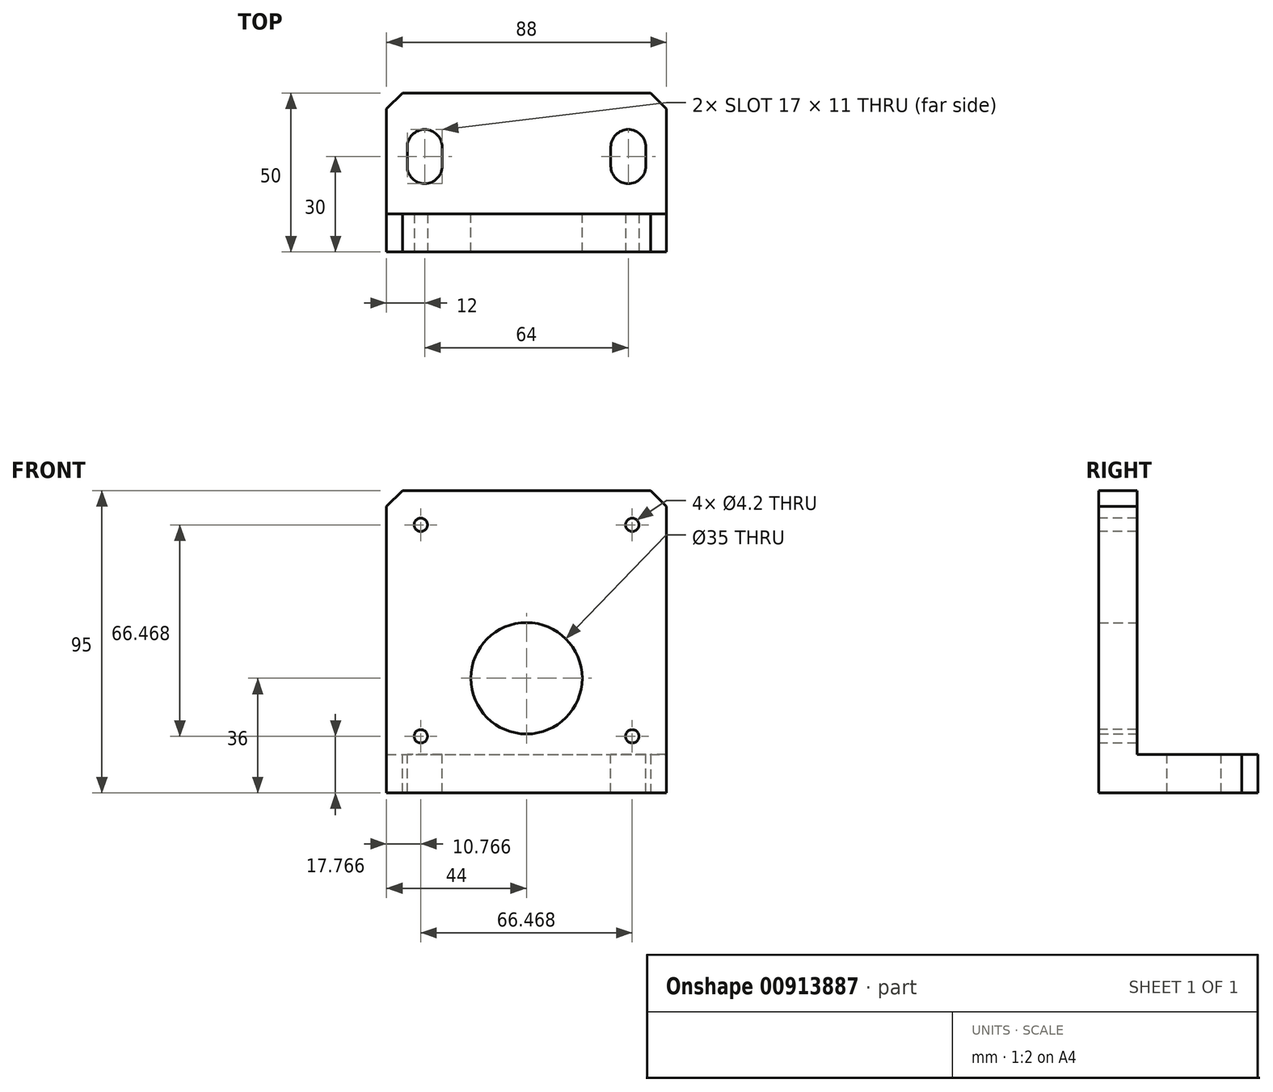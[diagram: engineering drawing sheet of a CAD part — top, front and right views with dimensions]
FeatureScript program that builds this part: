
annotation { "Feature Type Name" : "Feature", "Feature Type Description" : "" }
export const myFeature = defineFeature(function(context is Context, id is Id, definition is map)
    precondition{}
    {
        {
            var Q0;
            Q0=qCreatedBy(makeId("Front.planeOp"),FACE);
            var sketch = newSketch(context, id + "F0", { "sketchPlane" : qUnion([Q0])});
            skLineSegment(sketch, "E0.bottom", {"start": v(-44, 0) * mm, "end": v(44, 0) * mm});
            skLineSegment(sketch, "E0.top", {"start": v(-44, 95) * mm, "end": v(44, 95) * mm});
            skLineSegment(sketch, "E0.left", {"start": v(-44, 0) * mm, "end": v(-44, 95) * mm});
            skLineSegment(sketch, "E0.right", {"start": v(44, 0) * mm, "end": v(44, 95) * mm});
            skCircle(sketch, "E1", {"center": v(0, 36) * mm, "radius": 17.5 * mm});
            skSolve(sketch);
        }
        {
            var Q0;
            Q0 = qSketchRegion(id + "F0", true);
            extrude(context, id + "F1", {"entities" : qUnion([Q0]), "depth" : 12 * mm, "offsetDistance" : 25 * mm});
        }
        {
            var Q0;
            Q0=makeQuery(id+"F1.opExtrude","CAP_FACE",FACE,{"disambiguationData":[OSD([sQuery(id+"F0.wireOp",EDGE,"E0.bottom"),sQuery(id+"F0.wireOp",EDGE,"E0.top"),sQuery(id+"F0.wireOp",EDGE,"E0.left"),sQuery(id+"F0.wireOp",EDGE,"E0.right"),sQuery(id+"F0.wireOp",EDGE,"E1")])],"isStart":true});
            var sketch = newSketch(context, id + "F2", { "sketchPlane" : qUnion([Q0])});
            skLineSegment(sketch, "E2.bottom", {"start": v(44, 0) * mm, "end": v(-44, 0) * mm});
            skLineSegment(sketch, "E2.top", {"start": v(44, 12) * mm, "end": v(-44, 12) * mm});
            skLineSegment(sketch, "E2.left", {"start": v(44, 0) * mm, "end": v(44, 12) * mm});
            skLineSegment(sketch, "E2.right", {"start": v(-44, 0) * mm, "end": v(-44, 12) * mm});
            skSolve(sketch);
        }
        {
            var Q0;
            Q0 = qSketchRegion(id + "F2", true);
            extrude(context, id + "F3", {"entities" : qUnion([Q0]), "operationType" : NewBodyOperationType.ADD, "depth" : 38 * mm, "offsetDistance" : 25 * mm});
        }
        {
            var Q0;
            Q0=makeQuery(id+"F3.opExtrude","SWEPT_FACE",FACE,{"disambiguationData":[OSD([sQuery(id+"F2.wireOp",EDGE,"E2.top")])]});
            var sketch = newSketch(context, id + "F4", { "sketchPlane" : qUnion([Q0])});
            skLineSegment(sketch, "E3", {"start": v(32, 15) * mm, "end": v(32, 21) * mm, "construction": true});
            skLineSegment(sketch, "E4.0", {"start": v(37.5, 15) * mm, "end": v(37.5, 21) * mm});
            skLineSegment(sketch, "E5.0", {"start": v(26.5, 15) * mm, "end": v(26.5, 21) * mm});
            skArc(sketch, "E6", {"start": v(26.5, 15) * mm, "mid": v(32, 9.5) * mm, "end": v(37.5, 15) * mm});
            skArc(sketch, "E7", {"start": v(26.5, 21) * mm, "mid": v(32, 26.5) * mm, "end": v(37.5, 21) * mm});
            skLineSegment(sketch, "E8", {"start": v(0, 0) * mm, "end": v(0, 38) * mm, "construction": true});
            skLineSegment(sketch, "E9.MirrorCS", {"start": v(-26.5, 15) * mm, "end": v(-26.5, 21) * mm});
            skLineSegment(sketch, "E10.MirrorCS", {"start": v(-32, 15) * mm, "end": v(-32, 21) * mm, "construction": true});
            skLineSegment(sketch, "E11.MirrorCS", {"start": v(-37.5, 15) * mm, "end": v(-37.5, 21) * mm});
            skArc(sketch, "E12.MirrorCS", {"start": v(-26.5, 15) * mm, "mid": v(-32, 9.5) * mm, "end": v(-37.5, 15) * mm});
            skArc(sketch, "E13.MirrorCS", {"start": v(-26.5, 21) * mm, "mid": v(-32, 26.5) * mm, "end": v(-37.5, 21) * mm});
            skSolve(sketch);
        }
        {
            var Q0;
            Q0 = qSketchRegion(id + "F4", true);
            extrude(context, id + "F5", {"entities" : qUnion([Q0]), "operationType" : NewBodyOperationType.REMOVE, "endBound" : BoundingType.UP_TO_NEXT, "oppositeDirection" : true, "depth" : 25 * mm, "offsetDistance" : 25 * mm});
        }
        {
            var Q0;
            Q0=makeQuery(id+"F1.opExtrude","CAP_FACE",FACE,{"disambiguationData":[OSD([sQuery(id+"F0.wireOp",EDGE,"E0.bottom"),sQuery(id+"F0.wireOp",EDGE,"E0.top"),sQuery(id+"F0.wireOp",EDGE,"E0.left"),sQuery(id+"F0.wireOp",EDGE,"E0.right"),sQuery(id+"F0.wireOp",EDGE,"E1")])],"isStart":false});
            var sketch = newSketch(context, id + "F6", { "sketchPlane" : qUnion([Q0])});
            skCircle(sketch, "E14", {"center": v(0, 51) * mm, "radius": 47 * mm, "construction": true});
            skLineSegment(sketch, "E15", {"start": v(0, 51) * mm, "end": v(-33.23, 84.23) * mm, "construction": true});
            skPoint(sketch, "E16", {"position": v(-33.23, 84.23) * mm});
            skPoint(sketch, "E17.1.0", {"position": v(33.23, 84.23) * mm});
            skPoint(sketch, "E17.2.0", {"position": v(33.23, 17.77) * mm});
            skPoint(sketch, "E17.3.0", {"position": v(-33.23, 17.77) * mm});
            skLineSegment(sketch, "E17.anchor2", {"start": v(0, 51) * mm, "end": v(-33.23, 17.77) * mm, "construction": true});
            skSolve(sketch);
        }
        {
            var Q0;
            Q0=sQuery(id+"F6.wireOp",VERTEX,"E16");
            var Q1;
            Q1=sQuery(id+"F6.wireOp",VERTEX,"E17.1.0");
            var Q2;
            Q2=sQuery(id+"F6.wireOp",VERTEX,"E17.2.0");
            var Q3;
            Q3=sQuery(id+"F6.wireOp",VERTEX,"E17.3.0");
            var Q4;
            Q4=makeQuery(id+"F1.opExtrude","SWEPT_BODY",BODY,{"disambiguationData":[OSD([sQuery(id+"F0.wireOp",EDGE,"E0.bottom"),sQuery(id+"F0.wireOp",EDGE,"E0.top"),sQuery(id+"F0.wireOp",EDGE,"E0.left"),sQuery(id+"F0.wireOp",EDGE,"E0.right"),sQuery(id+"F0.wireOp",EDGE,"E1")])]});
            hole(context, id + "F7", {"style" : HoleStyle.SIMPLE, "endStyle" : HoleEndStyle.BLIND, "standardTappedOrClearance" : lookupTablePath({ "standard" : "ISO", "engagement" : "75%", "pitch" : "0.8 mm", "size" : "M5", "type" : "Tapped" }), "standardBlindInLast" : lookupTablePath({ "standard" : "ISO", "engagement" : "75%", "pitch" : "0.8 mm", "size" : "M5", "type" : "Tapped" }), "holeDiameter" : 4.2 * mm, "majorDiameter" : 5 * mm, "showTappedDepth" : true, "holeDepth" : 12 * mm, "isTappedThrough" : true, "tappedDepth" : 9.6 * mm, "tapClearance" : 3, "startFromSketch" : true, "locations" : qUnion([Q0, Q1, Q2, Q3]), "scope" : qUnion([Q4])});
        }
        {
            var Q0;
            Q0=makeQuery(id+"F1.opExtrude","SWEPT_EDGE",EDGE,{"disambiguationData":[OSD([sQuery(id+"F0.wireOp",EDGE,"E0.top"),sQuery(id+"F0.wireOp",EDGE,"E0.left")])]});
            var Q1;
            Q1=makeQuery(id+"F1.opExtrude","SWEPT_EDGE",EDGE,{"disambiguationData":[OSD([sQuery(id+"F0.wireOp",EDGE,"E0.top"),sQuery(id+"F0.wireOp",EDGE,"E0.right")])]});
            var Q2;
            Q2=makeQuery(id+"F3.opExtrude","CAP_EDGE",EDGE,{"disambiguationData":[OSD([sQuery(id+"F2.wireOp",EDGE,"E2.left")])],"isStart":false});
            var Q3;
            Q3=makeQuery(id+"F3.opExtrude","CAP_EDGE",EDGE,{"disambiguationData":[OSD([sQuery(id+"F2.wireOp",EDGE,"E2.right")])],"isStart":false});
            chamfer(context, id + "F8", {"entities" : qUnion([Q0, Q1, Q2, Q3]), "width" : 5 * mm, "tangentPropagation" : true});
        }
    });
